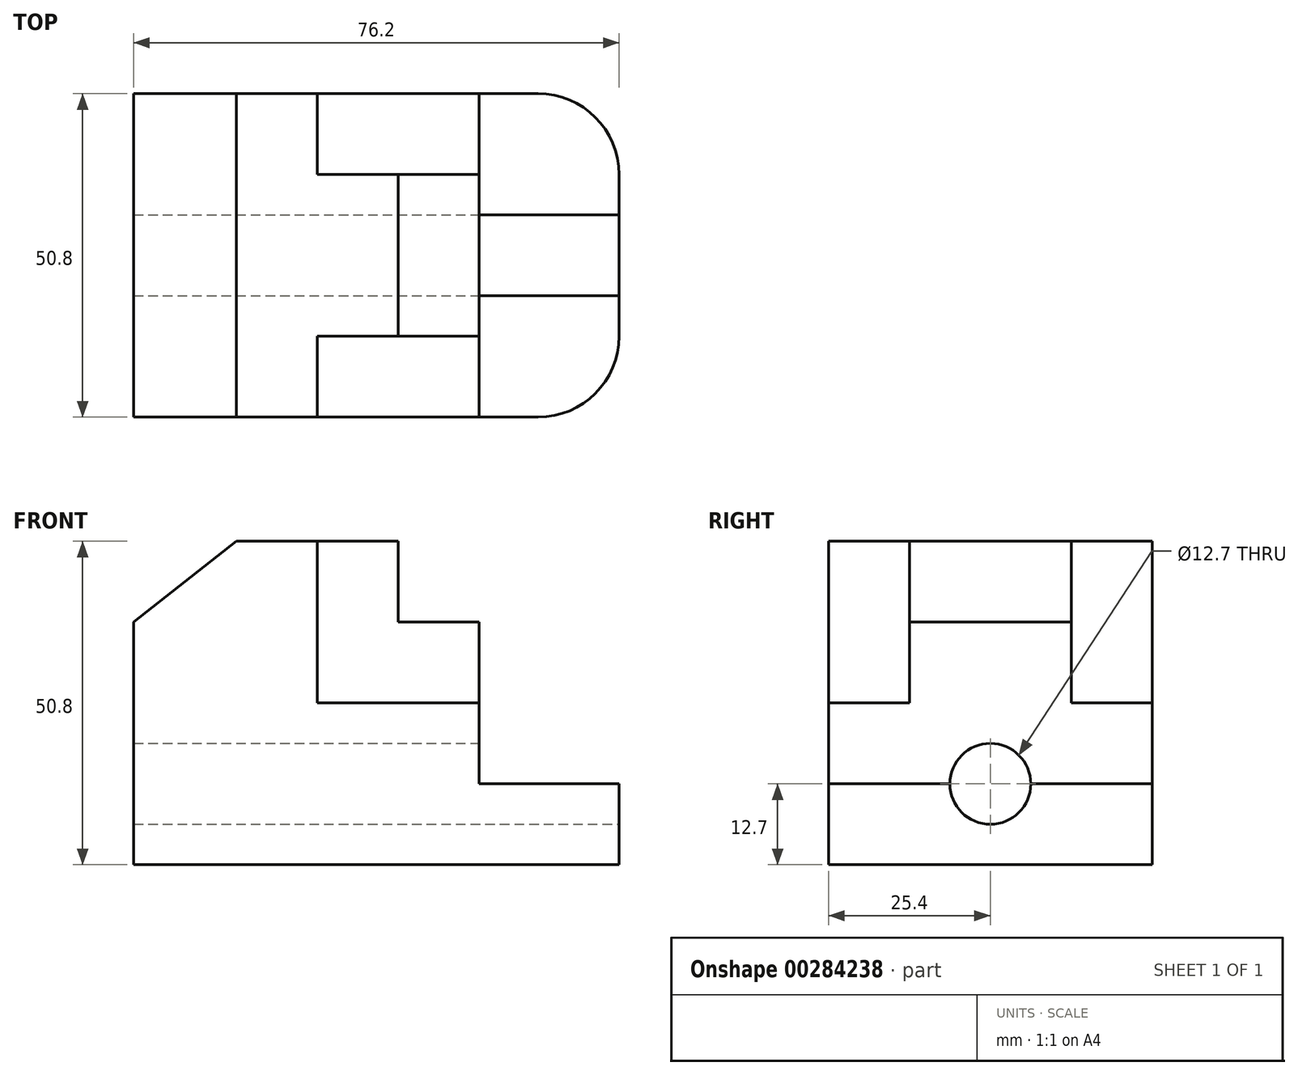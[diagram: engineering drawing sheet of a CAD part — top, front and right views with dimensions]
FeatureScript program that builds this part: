
annotation { "Feature Type Name" : "Feature", "Feature Type Description" : "" }
export const myFeature = defineFeature(function(context is Context, id is Id, definition is map)
    precondition{}
    {
        {
            var Q0;
            Q0=qCreatedBy(makeId("Front.planeOp"),FACE);
            var sketch = newSketch(context, id + "F0", { "sketchPlane" : qUnion([Q0])});
            skLineSegment(sketch, "E0", {"start": v(0, 0) * mm, "end": v(0, 38.1) * mm});
            skLineSegment(sketch, "E1", {"start": v(0, 38.1) * mm, "end": v(16.16, 50.8) * mm});
            skLineSegment(sketch, "E2", {"start": v(16.16, 50.8) * mm, "end": v(41.56, 50.8) * mm});
            skLineSegment(sketch, "E3", {"start": v(41.56, 50.8) * mm, "end": v(41.56, 38.1) * mm});
            skLineSegment(sketch, "E4", {"start": v(41.56, 38.1) * mm, "end": v(54.26, 38.1) * mm});
            skLineSegment(sketch, "E5", {"start": v(54.26, 38.1) * mm, "end": v(54.26, 12.7) * mm});
            skLineSegment(sketch, "E6", {"start": v(54.26, 12.7) * mm, "end": v(76.2, 12.7) * mm});
            skLineSegment(sketch, "E7", {"start": v(76.2, 12.7) * mm, "end": v(76.2, 0) * mm});
            skLineSegment(sketch, "E8", {"start": v(76.2, 0) * mm, "end": v(0, 0) * mm});
            skSolve(sketch);
        }
        {
            var Q0;
            Q0=makeQuery(id+"F0.imprint","IMPRINT",FACE,{"disambiguationData":[TD([[makeQuery(id+"F0.imprint","IMPRINT",EDGE,{"derivedFrom":sQuery(id+"F0.wireOp",EDGE,"E0")}),-1.0]])]});
            extrude(context, id + "F1", {"entities" : qUnion([Q0]), "endBound" : BoundingType.SYMMETRIC, "depth" : 50.8 * mm});
        }
        {
            var Q0;
            Q0=makeQuery(id+"F1.opExtrude","SWEPT_FACE",FACE,{"disambiguationData":[OSD([sQuery(id+"F0.wireOp",EDGE,"E5")])]});
            var sketch = newSketch(context, id + "F2", { "sketchPlane" : qUnion([Q0])});
            skCircle(sketch, "E9", {"center": v(0, 12.7) * mm, "radius": 6.35 * mm});
            skSolve(sketch);
        }
        {
            var Q0;
            Q0 = qSketchRegion(id + "F2", true);
            extrude(context, id + "F3", {"entities" : qUnion([Q0]), "operationType" : NewBodyOperationType.REMOVE, "endBound" : BoundingType.THROUGH_ALL, "oppositeDirection" : true, "depth" : 25.4 * mm});
        }
        {
            var Q0;
            Q0=makeQuery(id+"F1.opExtrude","SWEPT_FACE",FACE,{"disambiguationData":[OSD([sQuery(id+"F0.wireOp",EDGE,"E7")])]});
            var sketch = newSketch(context, id + "F4", { "sketchPlane" : qUnion([Q0])});
            skCircle(sketch, "E10", {"center": v(0, 12.7) * mm, "radius": 6.35 * mm});
            skSolve(sketch);
        }
        {
            var Q0;
            {var subQ0=sQuery(id+"F4.wireOp",EDGE,"E10");var subQ1=makeQuery(id+"F1.opExtrude","SWEPT_EDGE",EDGE,{"disambiguationData":[OSD([sQuery(id+"F0.wireOp",EDGE,"E6"),sQuery(id+"F0.wireOp",EDGE,"E7")])]});var subQ2=makeQuery(id+"F4.imprint","INTERSECT",VERTEX,{"disambiguationData":[OD(0.0)],"derivedFrom":[subQ1,subQ0]});Q0=makeQuery(id+"F4.imprint","IMPRINT",FACE,{"disambiguationData":[TD([[makeQuery(id+"F4.imprint","IMPRINT",EDGE,{"disambiguationData":[TD([[subQ2,1.0]])],"derivedFrom":subQ0}),1.0]])]});}
            extrude(context, id + "F5", {"entities" : qUnion([Q0]), "operationType" : NewBodyOperationType.REMOVE, "endBound" : BoundingType.THROUGH_ALL, "oppositeDirection" : true, "depth" : 25.4 * mm});
        }
        {
            var Q0;
            Q0=makeQuery(id+"F1.opExtrude","CAP_FACE",FACE,{"disambiguationData":[OSD([sQuery(id+"F0.wireOp",EDGE,"E0"),sQuery(id+"F0.wireOp",EDGE,"E1"),sQuery(id+"F0.wireOp",EDGE,"E2"),sQuery(id+"F0.wireOp",EDGE,"E3"),sQuery(id+"F0.wireOp",EDGE,"E4"),sQuery(id+"F0.wireOp",EDGE,"E5"),sQuery(id+"F0.wireOp",EDGE,"E6"),sQuery(id+"F0.wireOp",EDGE,"E7"),sQuery(id+"F0.wireOp",EDGE,"E8")])],"isStart":false});
            var sketch = newSketch(context, id + "F6", { "sketchPlane" : qUnion([Q0])});
            skLineSegment(sketch, "E11", {"start": v(28.86, 50.8) * mm, "end": v(28.86, 25.4) * mm});
            skLineSegment(sketch, "E12", {"start": v(28.86, 25.4) * mm, "end": v(54.26, 25.4) * mm});
            skLineSegment(sketch, "E13", {"start": v(54.26, 25.4) * mm, "end": v(54.26, 38.1) * mm});
            skLineSegment(sketch, "E14", {"start": v(54.26, 38.1) * mm, "end": v(41.56, 38.1) * mm});
            skLineSegment(sketch, "E15", {"start": v(41.56, 38.1) * mm, "end": v(41.56, 50.8) * mm});
            skLineSegment(sketch, "E16", {"start": v(41.56, 50.8) * mm, "end": v(28.86, 50.8) * mm});
            skSolve(sketch);
        }
        {
            var Q0;
            Q0 = qSketchRegion(id + "F6", true);
            extrude(context, id + "F7", {"entities" : qUnion([Q0]), "operationType" : NewBodyOperationType.REMOVE, "oppositeDirection" : true, "depth" : 12.7 * mm});
        }
        {
            var Q0;
            Q0=makeQuery(id+"F1.opExtrude","CAP_FACE",FACE,{"disambiguationData":[OSD([sQuery(id+"F0.wireOp",EDGE,"E0"),sQuery(id+"F0.wireOp",EDGE,"E1"),sQuery(id+"F0.wireOp",EDGE,"E2"),sQuery(id+"F0.wireOp",EDGE,"E3"),sQuery(id+"F0.wireOp",EDGE,"E4"),sQuery(id+"F0.wireOp",EDGE,"E5"),sQuery(id+"F0.wireOp",EDGE,"E6"),sQuery(id+"F0.wireOp",EDGE,"E7"),sQuery(id+"F0.wireOp",EDGE,"E8")])],"isStart":true});
            var sketch = newSketch(context, id + "F8", { "sketchPlane" : qUnion([Q0])});
            skLineSegment(sketch, "E17", {"start": v(-28.86, 50.8) * mm, "end": v(-28.86, 25.4) * mm});
            skLineSegment(sketch, "E18", {"start": v(-28.86, 25.4) * mm, "end": v(-54.26, 25.4) * mm});
            skLineSegment(sketch, "E19", {"start": v(-54.26, 25.4) * mm, "end": v(-54.26, 38.1) * mm});
            skLineSegment(sketch, "E20", {"start": v(-54.26, 38.1) * mm, "end": v(-41.56, 38.1) * mm});
            skLineSegment(sketch, "E21", {"start": v(-41.56, 38.1) * mm, "end": v(-41.56, 50.8) * mm});
            skLineSegment(sketch, "E22", {"start": v(-41.56, 50.8) * mm, "end": v(-28.86, 50.8) * mm});
            skSolve(sketch);
        }
        {
            var Q0;
            Q0 = qSketchRegion(id + "F8", true);
            extrude(context, id + "F9", {"entities" : qUnion([Q0]), "operationType" : NewBodyOperationType.REMOVE, "oppositeDirection" : true, "depth" : 12.7 * mm});
        }
        {
            var Q0;
            Q0=makeQuery(id+"F1.opExtrude","CAP_EDGE",EDGE,{"disambiguationData":[OSD([sQuery(id+"F0.wireOp",EDGE,"E7")])],"isStart":true});
            var Q1;
            Q1=makeQuery(id+"F1.opExtrude","CAP_EDGE",EDGE,{"disambiguationData":[OSD([sQuery(id+"F0.wireOp",EDGE,"E7")])],"isStart":false});
            fillet(context, id + "F10", {"entities" : qUnion([Q0, Q1]), "radius" : 12.7 * mm, "tangentPropagation" : true, "allowEdgeOverflow" : false});
        }
    });
